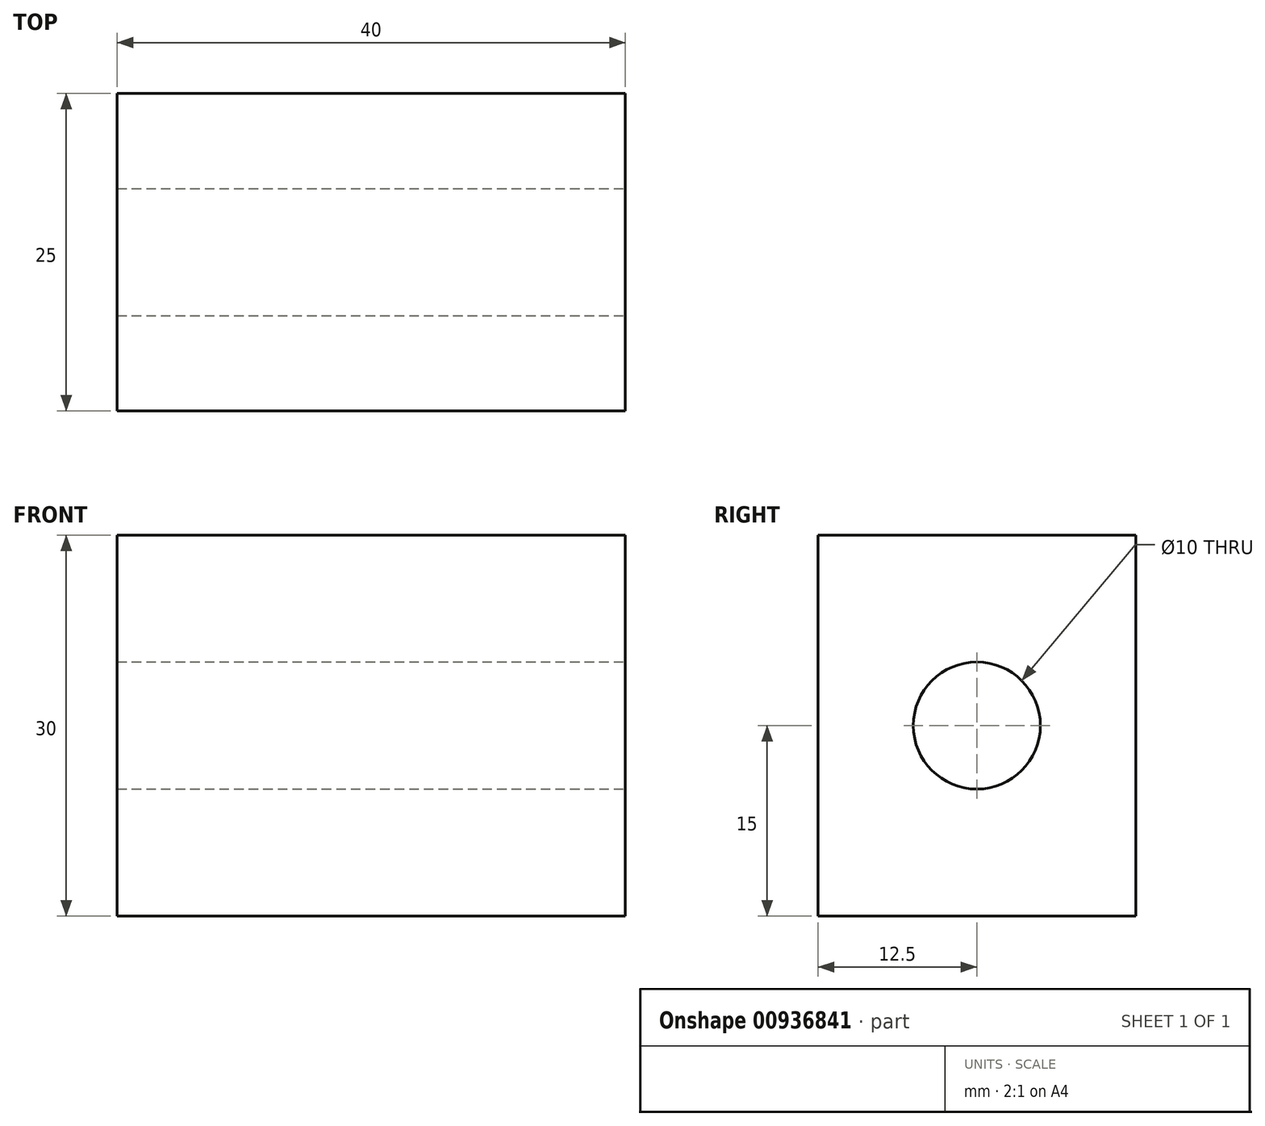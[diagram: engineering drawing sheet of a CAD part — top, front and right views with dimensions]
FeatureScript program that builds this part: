
annotation { "Feature Type Name" : "Feature", "Feature Type Description" : "" }
export const myFeature = defineFeature(function(context is Context, id is Id, definition is map)
    precondition{}
    {
        {
            var Q0;
            Q0=qCreatedBy(makeId("Front.planeOp"),FACE);
            var sketch = newSketch(context, id + "F0", { "sketchPlane" : qUnion([Q0])});
            skLineSegment(sketch, "E0.bottom", {"start": v(-20, 15) * mm, "end": v(20, 15) * mm});
            skLineSegment(sketch, "E0.top", {"start": v(-20, -15) * mm, "end": v(20, -15) * mm});
            skLineSegment(sketch, "E0.left", {"start": v(-20, 15) * mm, "end": v(-20, -15) * mm});
            skLineSegment(sketch, "E0.right", {"start": v(20, 15) * mm, "end": v(20, -15) * mm});
            skSolve(sketch);
        }
        {
            var Q0;
            Q0 = qSketchRegion(id + "F0", true);
            extrude(context, id + "F1", {"entities" : qUnion([Q0]), "endBound" : BoundingType.SYMMETRIC, "depth" : 25 * mm, "offsetDistance" : 25 * mm});
        }
        {
            var Q0;
            Q0=makeQuery(id+"F1.opExtrude","SWEPT_FACE",FACE,{"disambiguationData":[OSD([sQuery(id+"F0.wireOp",EDGE,"E0.right")])]});
            var sketch = newSketch(context, id + "F2", { "sketchPlane" : qUnion([Q0])});
            skCircle(sketch, "E1", {"center": v(0, 0) * mm, "radius": 5 * mm});
            skSolve(sketch);
        }
        {
            var Q0;
            Q0 = qSketchRegion(id + "F2", true);
            extrude(context, id + "F3", {"entities" : qUnion([Q0]), "operationType" : NewBodyOperationType.REMOVE, "oppositeDirection" : true, "depth" : 58 * mm, "offsetDistance" : 25 * mm});
        }
    });
